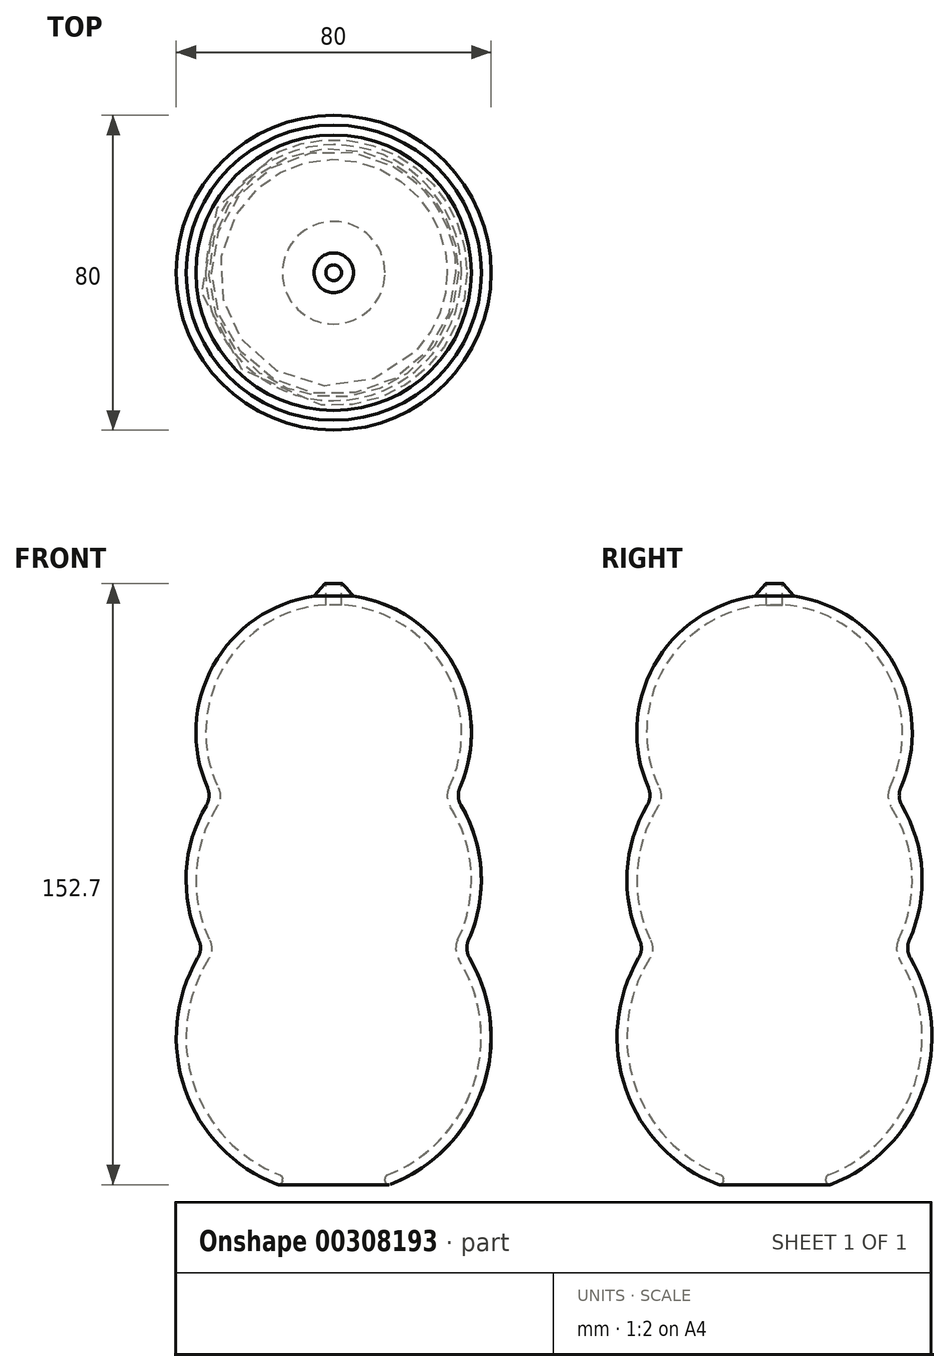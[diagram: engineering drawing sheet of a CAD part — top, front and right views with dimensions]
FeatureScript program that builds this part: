
annotation { "Feature Type Name" : "Feature", "Feature Type Description" : "" }
export const myFeature = defineFeature(function(context is Context, id is Id, definition is map)
    precondition{}
    {
        {
            var Q0;
            Q0=qCreatedBy(makeId("Front.planeOp"),FACE);
            var sketch = newSketch(context, id + "F0", { "sketchPlane" : qUnion([Q0])});
            skArc(sketch, "E0", {"start": v(-34.52, 20.2) * mm, "mid": v(-38.57, -10.59) * mm, "end": v(-19.36, -35) * mm});
            skArc(sketch, "E1", {"start": v(-32.35, 58.97) * mm, "mid": v(-37.44, 42.1) * mm, "end": v(-34.27, 24.77) * mm});
            skArc(sketch, "E2", {"start": v(-14.18, 109.5) * mm, "mid": v(-32.62, 90.2) * mm, "end": v(-32.08, 63.5) * mm});
            skPoint(sketch, "E3.orphan", {"position": v(0, -40) * mm});
            skPoint(sketch, "E4.orphan", {"position": v(0, 112.5) * mm});
            skPoint(sketch, "E5.end.orphan", {"position": v(0, -37.5) * mm});
            skArc(sketch, "E6", {"start": v(-31.77, 19.92) * mm, "mid": v(-35.5, -12.08) * mm, "end": v(-13.03, -35.16) * mm});
            skArc(sketch, "E7", {"start": v(-29.6, 58.67) * mm, "mid": v(-34.95, 41.96) * mm, "end": v(-31.5, 24.76) * mm});
            skArc(sketch, "E8", {"start": v(-2, 109.94) * mm, "mid": v(-28.01, 93.98) * mm, "end": v(-29.32, 63.49) * mm});
            skArc(sketch, "E9", {"start": v(-34.52, 20.2) * mm, "mid": v(-37.51, -13.9) * mm, "end": v(-13.03, -37.82) * mm});
            skArc(sketch, "E10", {"start": v(-2, 112.44) * mm, "mid": v(-29.82, 95.83) * mm, "end": v(-32.08, 63.5) * mm});
            skLineSegment(sketch, "E11", {"start": v(0, 112.5) * mm, "end": v(0, -40) * mm});
            skLineSegment(sketch, "E12", {"start": v(-2, 109.94) * mm, "end": v(-2, 112.44) * mm});
            skPoint(sketch, "E13.end.orphan", {"position": v(-2, 110.06) * mm});
            skLineSegment(sketch, "E14", {"start": v(-13.03, -35.16) * mm, "end": v(-13.03, -37.82) * mm});
            skPoint(sketch, "E15.end.orphan", {"position": v(-13.03, -39.75) * mm});
            skLineSegment(sketch, "E16", {"start": v(-13.03, -35.16) * mm, "end": v(0, -37.5) * mm, "construction": true});
            skLineSegment(sketch, "E17", {"start": v(-4.97, 112.18) * mm, "end": v(-2.3, 115.25) * mm});
            skLineSegment(sketch, "E18", {"start": v(-2, 115.14) * mm, "end": v(-2, 112.44) * mm});
            skPoint(sketch, "E19.visualSharp", {"position": v(-2, 115.6) * mm});
            skArc(sketch, "E19.filletArc", {"start": v(-2, 115.14) * mm, "mid": v(-2.11, 115.3) * mm, "end": v(-2.3, 115.25) * mm});
            skLineSegment(sketch, "E20", {"start": v(-4.96, 112.15) * mm, "end": v(-4.96, 112.15) * mm});
            skPoint(sketch, "E21.orphan", {"position": v(-5, 112.14) * mm});
            skArc(sketch, "E22", {"start": v(-5.02, 112.14) * mm, "mid": v(-5, 112.16) * mm, "end": v(-4.97, 112.18) * mm});
            skPoint(sketch, "E23.visualSharp", {"position": v(-33.12, 22.42) * mm});
            skArc(sketch, "E23.filletArc", {"start": v(-34.52, 20.2) * mm, "mid": v(-33.84, 22.46) * mm, "end": v(-34.27, 24.77) * mm});
            skPoint(sketch, "E24.visualSharp", {"position": v(-30.96, 61.17) * mm});
            skArc(sketch, "E24.filletArc", {"start": v(-32.35, 58.97) * mm, "mid": v(-31.67, 61.2) * mm, "end": v(-32.08, 63.5) * mm});
            skPoint(sketch, "E25.visualSharp", {"position": v(-30.17, 22.27) * mm});
            skArc(sketch, "E25.filletArc", {"start": v(-31.77, 19.92) * mm, "mid": v(-31.01, 22.3) * mm, "end": v(-31.5, 24.76) * mm});
            skPoint(sketch, "E26.visualSharp", {"position": v(-28, 61) * mm});
            skArc(sketch, "E26.filletArc", {"start": v(-29.6, 58.67) * mm, "mid": v(-28.84, 61.04) * mm, "end": v(-29.32, 63.49) * mm});
            skPoint(sketch, "E27.end.orphan", {"position": v(-5, 110.06) * mm});
            skSolve(sketch);
        }
        {
            var Q0;
            {var subQ2=sQuery(id+"F0.wireOp",EDGE,"E1");Q0=makeQuery(id+"F0.imprint","IMPRINT",FACE,{"disambiguationData":[TD([[makeQuery(id+"F0.imprint","IMPRINT",EDGE,{"derivedFrom":subQ2}),1.0]])]});}
            var Q1;
            {var subQ2=sQuery(id+"F0.wireOp",EDGE,"E17");Q1=makeQuery(id+"F0.imprint","IMPRINT",FACE,{"disambiguationData":[TD([[makeQuery(id+"F0.imprint","IMPRINT",EDGE,{"derivedFrom":subQ2}),-1.0]])]});}
            var Q2;
            Q2=sQuery(id+"F0.wireOp",EDGE,"E11");
            revolve(context, id + "F1", {"entities" : qUnion([Q0, Q1]), "axis" : qUnion([Q2]), "revolveType" : RevolveType.FULL});
        }
        {
            var Q0;
            Q0=makeQuery(id+"F1.opRevolve","SWEPT_EDGE",EDGE,{"disambiguationData":[OSD([sQuery(id+"F0.wireOp",EDGE,"E6"),sQuery(id+"F0.wireOp",EDGE,"E14")])]});
            fillet(context, id + "F2", {"entities" : qUnion([Q0]), "radius" : 1 * mm, "tangentPropagation" : true, "allowEdgeOverflow" : false});
        }
        {
            var Q0;
            Q0=makeQuery(id+"F1.opRevolve","SWEPT_EDGE",EDGE,{"disambiguationData":[OSD([sQuery(id+"F0.wireOp",EDGE,"E9"),sQuery(id+"F0.wireOp",EDGE,"E14")])]});
            fillet(context, id + "F3", {"entities" : qUnion([Q0]), "radius" : 1 * mm, "tangentPropagation" : true, "allowEdgeOverflow" : false});
        }
    });
